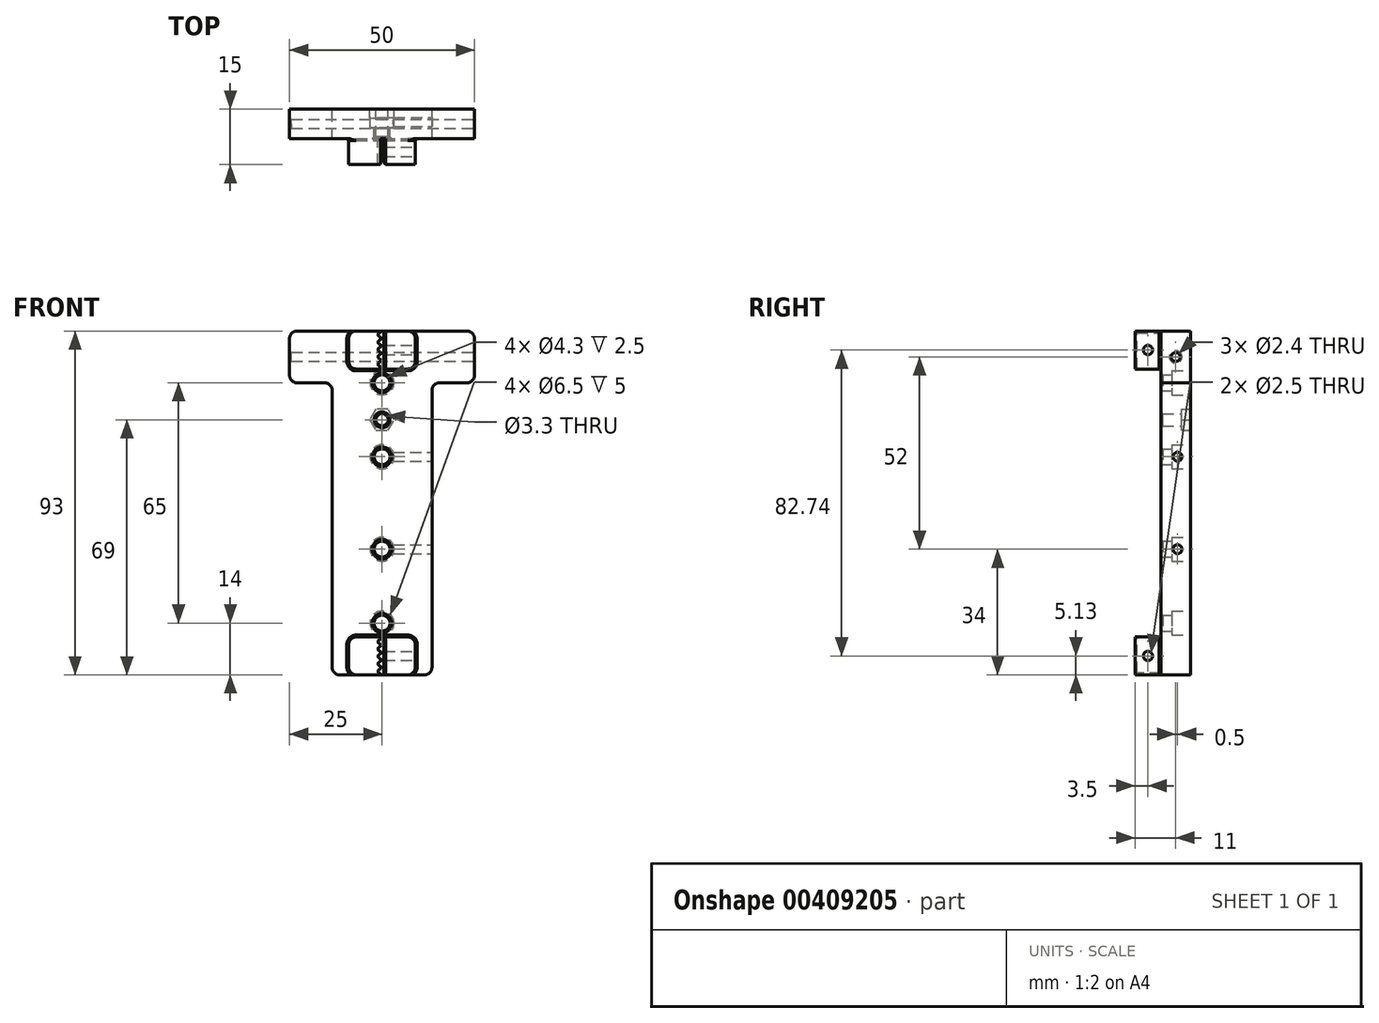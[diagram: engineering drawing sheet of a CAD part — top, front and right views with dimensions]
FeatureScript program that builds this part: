
annotation { "Feature Type Name" : "Feature", "Feature Type Description" : "" }
export const myFeature = defineFeature(function(context is Context, id is Id, definition is map)
    precondition{}
    {
        {
            var Q0;
            Q0=qCreatedBy(makeId("Front.planeOp"),FACE);
            var sketch = newSketch(context, id + "F0", { "sketchPlane" : qUnion([Q0])});
            skLineSegment(sketch, "E0.bottom", {"start": v(13.5, -86) * mm, "end": v(-13.5, -86) * mm});
            skLineSegment(sketch, "E0.left", {"start": v(13.5, -86) * mm, "end": v(13.5, -7) * mm});
            skLineSegment(sketch, "E0.right", {"start": v(-13.5, -86) * mm, "end": v(-13.5, -7) * mm});
            skLineSegment(sketch, "E1.top", {"start": v(-25, 7) * mm, "end": v(25, 7) * mm});
            skLineSegment(sketch, "E1.left", {"start": v(-25, -7) * mm, "end": v(-25, 7) * mm});
            skLineSegment(sketch, "E1.right", {"start": v(25, -7) * mm, "end": v(25, 7) * mm});
            skPoint(sketch, "E1.middle", {"position": v(0, 0) * mm});
            skCircle(sketch, "E2", {"center": v(0, -7) * mm, "radius": 2.15 * mm});
            skCircle(sketch, "E3", {"center": v(0, -17) * mm, "radius": 1.65 * mm});
            skCircle(sketch, "E4", {"center": v(0, -27) * mm, "radius": 2.15 * mm});
            skCircle(sketch, "E5", {"center": v(0, -52) * mm, "radius": 2.15 * mm});
            skCircle(sketch, "E6", {"center": v(0, -72) * mm, "radius": 2.15 * mm});
            skLineSegment(sketch, "E7", {"start": v(-32.04, -39.5) * mm, "end": v(39, -39.5) * mm, "construction": true});
            skLineSegment(sketch, "E8", {"start": v(-25, -7) * mm, "end": v(-13.5, -7) * mm});
            skLineSegment(sketch, "E9", {"start": v(13.5, -7) * mm, "end": v(25, -7) * mm});
            skSolve(sketch);
        }
        {
            var Q0;
            Q0=makeQuery(id+"F0.imprint","IMPRINT",FACE,{"disambiguationData":[TD([[makeQuery(id+"F0.imprint","IMPRINT",EDGE,{"derivedFrom":sQuery(id+"F0.wireOp",EDGE,"E0.bottom")}),-1.0]])]});
            extrude(context, id + "F1", {"entities" : qUnion([Q0]), "depth" : 8 * mm, "offsetDistance" : 25 * mm, "symmetric" : true});
        }
        {
            var Q0;
            Q0=makeQuery(id+"F1.opExtrude","CAP_FACE",FACE,{"disambiguationData":[OSD([sQuery(id+"F0.wireOp",EDGE,"E0.bottom"),sQuery(id+"F0.wireOp",EDGE,"E0.left"),sQuery(id+"F0.wireOp",EDGE,"E0.right"),sQuery(id+"F0.wireOp",EDGE,"E1.top"),sQuery(id+"F0.wireOp",EDGE,"E1.left"),sQuery(id+"F0.wireOp",EDGE,"E1.right"),sQuery(id+"F0.wireOp",EDGE,"E2"),sQuery(id+"F0.wireOp",EDGE,"E3"),sQuery(id+"F0.wireOp",EDGE,"E4"),sQuery(id+"F0.wireOp",EDGE,"E5"),sQuery(id+"F0.wireOp",EDGE,"E6"),sQuery(id+"F0.wireOp",EDGE,"E8"),sQuery(id+"F0.wireOp",EDGE,"E9")])],"isStart":false});
            var sketch = newSketch(context, id + "F2", { "sketchPlane" : qUnion([Q0])});
            skLineSegment(sketch, "E10", {"start": v(0.48, 7) * mm, "end": v(0.48, 6) * mm});
            skLineSegment(sketch, "E11", {"start": v(-0.35, 7) * mm, "end": v(-0.35, 6.74) * mm});
            skArc(sketch, "E12", {"start": v(-0.35, 6.74) * mm, "mid": v(-0.4, 6.64) * mm, "end": v(-0.48, 6.6) * mm});
            skLineSegment(sketch, "E13", {"start": v(-1.63, 6) * mm, "end": v(0.48, 6) * mm, "construction": true});
            skArc(sketch, "E14", {"start": v(-1.1, 6) * mm, "mid": v(-1.02, 6.3) * mm, "end": v(-0.8, 6.5) * mm});
            skArc(sketch, "E15", {"start": v(-0.8, 6.5) * mm, "mid": v(-0.64, 6.56) * mm, "end": v(-0.48, 6.6) * mm});
            skArc(sketch, "E16.MirrorCS", {"start": v(-1.1, 6) * mm, "mid": v(-1.02, 5.7) * mm, "end": v(-0.8, 5.5) * mm});
            skArc(sketch, "E17.MirrorCS", {"start": v(-0.8, 5.5) * mm, "mid": v(-0.64, 5.44) * mm, "end": v(-0.48, 5.4) * mm});
            skArc(sketch, "E18.MirrorCS", {"start": v(-0.35, 5.26) * mm, "mid": v(-0.4, 5.36) * mm, "end": v(-0.48, 5.4) * mm});
            skLineSegment(sketch, "E19.MirrorCS", {"start": v(-0.35, 5) * mm, "end": v(-0.35, 5.26) * mm});
            skLineSegment(sketch, "E20.MirrorCS", {"start": v(0.48, 5) * mm, "end": v(0.48, 6) * mm});
            skLineSegment(sketch, "E21", {"start": v(-0.35, 5) * mm, "end": v(0.48, 5) * mm, "construction": true});
            skArc(sketch, "E22.MirrorCS", {"start": v(-0.35, 3.26) * mm, "mid": v(-0.4, 3.36) * mm, "end": v(-0.48, 3.4) * mm});
            skArc(sketch, "E23.MirrorCS", {"start": v(-0.8, 3.5) * mm, "mid": v(-0.64, 3.44) * mm, "end": v(-0.48, 3.4) * mm});
            skLineSegment(sketch, "E24.MirrorCS", {"start": v(-0.35, 5) * mm, "end": v(-0.35, 4.74) * mm});
            skArc(sketch, "E25.MirrorCS", {"start": v(-0.8, 4.5) * mm, "mid": v(-0.64, 4.56) * mm, "end": v(-0.48, 4.6) * mm});
            skArc(sketch, "E26.MirrorCS", {"start": v(-0.35, 4.74) * mm, "mid": v(-0.4, 4.64) * mm, "end": v(-0.48, 4.6) * mm});
            skLineSegment(sketch, "E27.MirrorCS", {"start": v(-0.35, 3) * mm, "end": v(-0.35, 3.26) * mm});
            skLineSegment(sketch, "E28.MirrorCS", {"start": v(-1.63, 4) * mm, "end": v(0.48, 4) * mm, "construction": true});
            skArc(sketch, "E29.MirrorCS", {"start": v(-1.1, 4) * mm, "mid": v(-1.02, 4.3) * mm, "end": v(-0.8, 4.5) * mm});
            skLineSegment(sketch, "E30.MirrorCS", {"start": v(0.48, 3) * mm, "end": v(0.48, 4) * mm});
            skArc(sketch, "E31.MirrorCS", {"start": v(-1.1, 4) * mm, "mid": v(-1.02, 3.7) * mm, "end": v(-0.8, 3.5) * mm});
            skLineSegment(sketch, "E32.MirrorCS", {"start": v(0.48, 5) * mm, "end": v(0.48, 4) * mm});
            skLineSegment(sketch, "E33", {"start": v(-0.35, 3) * mm, "end": v(0.48, 3) * mm, "construction": true});
            skLineSegment(sketch, "E34.MirrorCS", {"start": v(-0.35, 1) * mm, "end": v(-0.35, 0.74) * mm});
            skArc(sketch, "E35.MirrorCS", {"start": v(-0.35, -0.74) * mm, "mid": v(-0.4, -0.64) * mm, "end": v(-0.48, -0.6) * mm});
            skArc(sketch, "E36.MirrorCS", {"start": v(-0.35, 2.74) * mm, "mid": v(-0.4, 2.64) * mm, "end": v(-0.48, 2.6) * mm});
            skArc(sketch, "E37.MirrorCS", {"start": v(-0.35, 0.74) * mm, "mid": v(-0.4, 0.64) * mm, "end": v(-0.48, 0.6) * mm});
            skArc(sketch, "E38.MirrorCS", {"start": v(-0.8, -0.5) * mm, "mid": v(-0.64, -0.56) * mm, "end": v(-0.48, -0.6) * mm});
            skArc(sketch, "E39.MirrorCS", {"start": v(-0.35, 1.26) * mm, "mid": v(-0.4, 1.36) * mm, "end": v(-0.48, 1.4) * mm});
            skArc(sketch, "E40.MirrorCS", {"start": v(-0.8, 2.5) * mm, "mid": v(-0.64, 2.56) * mm, "end": v(-0.48, 2.6) * mm});
            skLineSegment(sketch, "E41.MirrorCS", {"start": v(-0.35, 3) * mm, "end": v(-0.35, 2.74) * mm});
            skLineSegment(sketch, "E42.MirrorCS", {"start": v(-0.35, 1) * mm, "end": v(-0.35, 1.26) * mm});
            skArc(sketch, "E43.MirrorCS", {"start": v(-0.8, 0.5) * mm, "mid": v(-0.64, 0.56) * mm, "end": v(-0.48, 0.6) * mm});
            skArc(sketch, "E44.MirrorCS", {"start": v(-0.8, 1.5) * mm, "mid": v(-0.64, 1.44) * mm, "end": v(-0.48, 1.4) * mm});
            skLineSegment(sketch, "E45.MirrorCS", {"start": v(-0.35, -1) * mm, "end": v(-0.35, -0.74) * mm});
            skArc(sketch, "E46.MirrorCS", {"start": v(-1.1, 0) * mm, "mid": v(-1.02, -0.3) * mm, "end": v(-0.8, -0.5) * mm});
            skLineSegment(sketch, "E47.MirrorCS", {"start": v(-1.63, 0) * mm, "end": v(0.48, 0) * mm, "construction": true});
            skLineSegment(sketch, "E48.MirrorCS", {"start": v(-0.35, 1) * mm, "end": v(0.48, 1) * mm, "construction": true});
            skLineSegment(sketch, "E49.MirrorCS", {"start": v(0.48, 1) * mm, "end": v(0.48, 2) * mm});
            skArc(sketch, "E50.MirrorCS", {"start": v(-1.1, 2) * mm, "mid": v(-1.02, 2.3) * mm, "end": v(-0.8, 2.5) * mm});
            skArc(sketch, "E51.MirrorCS", {"start": v(-1.1, 2) * mm, "mid": v(-1.02, 1.7) * mm, "end": v(-0.8, 1.5) * mm});
            skLineSegment(sketch, "E52.MirrorCS", {"start": v(0.48, 1) * mm, "end": v(0.48, 0) * mm});
            skArc(sketch, "E53.MirrorCS", {"start": v(-1.1, 0) * mm, "mid": v(-1.02, 0.3) * mm, "end": v(-0.8, 0.5) * mm});
            skLineSegment(sketch, "E54.MirrorCS", {"start": v(0.48, -1) * mm, "end": v(0.48, 0) * mm});
            skLineSegment(sketch, "E55.MirrorCS", {"start": v(0.48, 3) * mm, "end": v(0.48, 2) * mm});
            skLineSegment(sketch, "E56.MirrorCS", {"start": v(-1.63, 2) * mm, "end": v(0.48, 2) * mm, "construction": true});
            skLineSegment(sketch, "E57", {"start": v(-0.35, -1) * mm, "end": v(0.48, -1) * mm, "construction": true});
            skLineSegment(sketch, "E58.MirrorCS", {"start": v(-0.35, -3) * mm, "end": v(-0.35, -2.74) * mm});
            skArc(sketch, "E59.MirrorCS", {"start": v(-0.35, -1.26) * mm, "mid": v(-0.4, -1.36) * mm, "end": v(-0.48, -1.4) * mm});
            skArc(sketch, "E60.MirrorCS", {"start": v(-0.35, -2.74) * mm, "mid": v(-0.4, -2.64) * mm, "end": v(-0.48, -2.6) * mm});
            skLineSegment(sketch, "E61.MirrorCS", {"start": v(-0.35, -3) * mm, "end": v(-0.35, -3.26) * mm});
            skLineSegment(sketch, "E62.MirrorCS", {"start": v(-0.35, -1) * mm, "end": v(-0.35, -1.26) * mm});
            skArc(sketch, "E63.MirrorCS", {"start": v(-0.8, -2.5) * mm, "mid": v(-0.64, -2.56) * mm, "end": v(-0.48, -2.6) * mm});
            skArc(sketch, "E64.MirrorCS", {"start": v(-0.8, -1.5) * mm, "mid": v(-0.64, -1.44) * mm, "end": v(-0.48, -1.4) * mm});
            skLineSegment(sketch, "E65.MirrorCS", {"start": v(-0.35, -3) * mm, "end": v(0.48, -3) * mm, "construction": true});
            skLineSegment(sketch, "E66.MirrorCS", {"start": v(0.48, -3) * mm, "end": v(0.48, -2) * mm});
            skLineSegment(sketch, "E67.MirrorCS", {"start": v(-1.63, -2) * mm, "end": v(0.48, -2) * mm, "construction": true});
            skArc(sketch, "E68.MirrorCS", {"start": v(-1.1, -2) * mm, "mid": v(-1.02, -2.3) * mm, "end": v(-0.8, -2.5) * mm});
            skLineSegment(sketch, "E69.MirrorCS", {"start": v(0.48, -1) * mm, "end": v(0.48, -2) * mm});
            skArc(sketch, "E70.MirrorCS", {"start": v(-1.1, -2) * mm, "mid": v(-1.02, -1.7) * mm, "end": v(-0.8, -1.5) * mm});
            skLineSegment(sketch, "E71", {"start": v(0.48, 7) * mm, "end": v(9, 7) * mm});
            skLineSegment(sketch, "E72", {"start": v(9, 7) * mm, "end": v(9, -3.26) * mm});
            skLineSegment(sketch, "E73", {"start": v(9, -3.26) * mm, "end": v(0.48, -3.26) * mm});
            skLineSegment(sketch, "E74", {"start": v(-0.35, 7) * mm, "end": v(-9, 7) * mm});
            skLineSegment(sketch, "E75", {"start": v(-9, 7) * mm, "end": v(-9, -3.26) * mm});
            skLineSegment(sketch, "E76", {"start": v(-9, -3.26) * mm, "end": v(-0.35, -3.26) * mm});
            skLineSegment(sketch, "E77", {"start": v(0.48, -3) * mm, "end": v(0.48, -3.26) * mm});
            skLineSegment(sketch, "E78", {"start": v(-13.5, -39.5) * mm, "end": v(13.5, -39.5) * mm, "construction": true});
            skArc(sketch, "E79.MirrorCS", {"start": v(-0.35, -83.74) * mm, "mid": v(-0.4, -83.64) * mm, "end": v(-0.48, -83.6) * mm});
            skLineSegment(sketch, "E80.MirrorCS", {"start": v(-0.35, -84) * mm, "end": v(-0.35, -84.26) * mm});
            skArc(sketch, "E81.MirrorCS", {"start": v(-0.35, -84.26) * mm, "mid": v(-0.4, -84.36) * mm, "end": v(-0.48, -84.4) * mm});
            skArc(sketch, "E82.MirrorCS", {"start": v(-0.8, -83.5) * mm, "mid": v(-0.64, -83.56) * mm, "end": v(-0.48, -83.6) * mm});
            skLineSegment(sketch, "E83.MirrorCS", {"start": v(-0.35, -84) * mm, "end": v(-0.35, -83.74) * mm});
            skArc(sketch, "E84.MirrorCS", {"start": v(-0.8, -84.5) * mm, "mid": v(-0.64, -84.44) * mm, "end": v(-0.48, -84.4) * mm});
            skArc(sketch, "E85.MirrorCS", {"start": v(-0.35, -80.26) * mm, "mid": v(-0.4, -80.36) * mm, "end": v(-0.48, -80.4) * mm});
            skArc(sketch, "E86.MirrorCS", {"start": v(-0.35, -79.74) * mm, "mid": v(-0.4, -79.64) * mm, "end": v(-0.48, -79.6) * mm});
            skArc(sketch, "E87.MirrorCS", {"start": v(-0.8, -80.5) * mm, "mid": v(-0.64, -80.44) * mm, "end": v(-0.48, -80.4) * mm});
            skArc(sketch, "E88.MirrorCS", {"start": v(-0.8, -79.5) * mm, "mid": v(-0.64, -79.56) * mm, "end": v(-0.48, -79.6) * mm});
            skLineSegment(sketch, "E89.MirrorCS", {"start": v(-0.35, -80) * mm, "end": v(-0.35, -79.74) * mm});
            skLineSegment(sketch, "E90.MirrorCS", {"start": v(-0.35, -80) * mm, "end": v(-0.35, -80.26) * mm});
            skLineSegment(sketch, "E91.MirrorCS", {"start": v(-0.35, -78) * mm, "end": v(-0.35, -77.74) * mm});
            skLineSegment(sketch, "E92.MirrorCS", {"start": v(-0.35, -78) * mm, "end": v(-0.35, -78.26) * mm});
            skArc(sketch, "E93.MirrorCS", {"start": v(-0.35, -82.26) * mm, "mid": v(-0.4, -82.36) * mm, "end": v(-0.48, -82.4) * mm});
            skArc(sketch, "E94.MirrorCS", {"start": v(-0.8, -78.5) * mm, "mid": v(-0.64, -78.44) * mm, "end": v(-0.48, -78.4) * mm});
            skArc(sketch, "E95.MirrorCS", {"start": v(-0.35, -78.26) * mm, "mid": v(-0.4, -78.36) * mm, "end": v(-0.48, -78.4) * mm});
            skLineSegment(sketch, "E96.MirrorCS", {"start": v(-0.35, -82) * mm, "end": v(-0.35, -82.26) * mm});
            skArc(sketch, "E97.MirrorCS", {"start": v(-0.8, -82.5) * mm, "mid": v(-0.64, -82.44) * mm, "end": v(-0.48, -82.4) * mm});
            skArc(sketch, "E98.MirrorCS", {"start": v(-0.8, -85.5) * mm, "mid": v(-0.64, -85.56) * mm, "end": v(-0.48, -85.6) * mm});
            skArc(sketch, "E99.MirrorCS", {"start": v(-0.35, -77.74) * mm, "mid": v(-0.4, -77.64) * mm, "end": v(-0.48, -77.6) * mm});
            skArc(sketch, "E100.MirrorCS", {"start": v(-1.1, -83) * mm, "mid": v(-1.02, -83.3) * mm, "end": v(-0.8, -83.5) * mm});
            skArc(sketch, "E101.MirrorCS", {"start": v(-0.8, -77.5) * mm, "mid": v(-0.64, -77.56) * mm, "end": v(-0.48, -77.6) * mm});
            skLineSegment(sketch, "E102.MirrorCS", {"start": v(-0.35, -82) * mm, "end": v(-0.35, -81.74) * mm});
            skArc(sketch, "E103.MirrorCS", {"start": v(-0.8, -76.5) * mm, "mid": v(-0.64, -76.44) * mm, "end": v(-0.48, -76.4) * mm});
            skLineSegment(sketch, "E104.MirrorCS", {"start": v(0.48, -76) * mm, "end": v(0.48, -75.74) * mm});
            skLineSegment(sketch, "E105.MirrorCS", {"start": v(-0.35, -76) * mm, "end": v(-0.35, -75.74) * mm});
            skLineSegment(sketch, "E106.MirrorCS", {"start": v(-0.35, -84) * mm, "end": v(0.48, -84) * mm, "construction": true});
            skArc(sketch, "E107.MirrorCS", {"start": v(-0.8, -81.5) * mm, "mid": v(-0.64, -81.56) * mm, "end": v(-0.48, -81.6) * mm});
            skArc(sketch, "E108.MirrorCS", {"start": v(-1.1, -83) * mm, "mid": v(-1.02, -82.7) * mm, "end": v(-0.8, -82.5) * mm});
            skLineSegment(sketch, "E109.MirrorCS", {"start": v(-1.63, -83) * mm, "end": v(0.48, -83) * mm, "construction": true});
            skArc(sketch, "E110.MirrorCS", {"start": v(-0.35, -85.74) * mm, "mid": v(-0.4, -85.64) * mm, "end": v(-0.48, -85.6) * mm});
            skArc(sketch, "E111.MirrorCS", {"start": v(-1.1, -85) * mm, "mid": v(-1.02, -85.3) * mm, "end": v(-0.8, -85.5) * mm});
            skArc(sketch, "E112.MirrorCS", {"start": v(-1.1, -81) * mm, "mid": v(-1.02, -80.7) * mm, "end": v(-0.8, -80.5) * mm});
            skArc(sketch, "E113.MirrorCS", {"start": v(-1.1, -85) * mm, "mid": v(-1.02, -84.7) * mm, "end": v(-0.8, -84.5) * mm});
            skLineSegment(sketch, "E114.MirrorCS", {"start": v(-0.35, -76) * mm, "end": v(-0.35, -76.26) * mm});
            skLineSegment(sketch, "E115.MirrorCS", {"start": v(-0.35, -86) * mm, "end": v(-0.35, -85.74) * mm});
            skLineSegment(sketch, "E116.MirrorCS", {"start": v(-0.35, -76) * mm, "end": v(0.48, -76) * mm, "construction": true});
            skArc(sketch, "E117.MirrorCS", {"start": v(-0.35, -81.74) * mm, "mid": v(-0.4, -81.64) * mm, "end": v(-0.48, -81.6) * mm});
            skLineSegment(sketch, "E118.MirrorCS", {"start": v(0.48, -84) * mm, "end": v(0.48, -85) * mm});
            skArc(sketch, "E119.MirrorCS", {"start": v(-1.1, -77) * mm, "mid": v(-1.02, -77.3) * mm, "end": v(-0.8, -77.5) * mm});
            skArc(sketch, "E120.MirrorCS", {"start": v(-0.35, -76.26) * mm, "mid": v(-0.4, -76.36) * mm, "end": v(-0.48, -76.4) * mm});
            skArc(sketch, "E121.MirrorCS", {"start": v(-1.1, -77) * mm, "mid": v(-1.02, -76.7) * mm, "end": v(-0.8, -76.5) * mm});
            skLineSegment(sketch, "E122.MirrorCS", {"start": v(0.48, -84) * mm, "end": v(0.48, -83) * mm});
            skArc(sketch, "E123.MirrorCS", {"start": v(-1.1, -79) * mm, "mid": v(-1.02, -79.3) * mm, "end": v(-0.8, -79.5) * mm});
            skLineSegment(sketch, "E124.MirrorCS", {"start": v(0.48, -82) * mm, "end": v(0.48, -83) * mm});
            skArc(sketch, "E125.MirrorCS", {"start": v(-1.1, -79) * mm, "mid": v(-1.02, -78.7) * mm, "end": v(-0.8, -78.5) * mm});
            skLineSegment(sketch, "E126.MirrorCS", {"start": v(0.48, -82) * mm, "end": v(0.48, -81) * mm});
            skLineSegment(sketch, "E127.MirrorCS", {"start": v(-0.35, -80) * mm, "end": v(0.48, -80) * mm, "construction": true});
            skLineSegment(sketch, "E128.MirrorCS", {"start": v(0.48, -78) * mm, "end": v(0.48, -77) * mm});
            skLineSegment(sketch, "E129.MirrorCS", {"start": v(0.48, -76) * mm, "end": v(0.48, -77) * mm});
            skLineSegment(sketch, "E130.MirrorCS", {"start": v(0.48, -80) * mm, "end": v(0.48, -79) * mm});
            skLineSegment(sketch, "E131.MirrorCS", {"start": v(-1.63, -85) * mm, "end": v(0.48, -85) * mm, "construction": true});
            skLineSegment(sketch, "E132.MirrorCS", {"start": v(-0.35, -78) * mm, "end": v(0.48, -78) * mm, "construction": true});
            skArc(sketch, "E133.MirrorCS", {"start": v(-1.1, -81) * mm, "mid": v(-1.02, -81.3) * mm, "end": v(-0.8, -81.5) * mm});
            skLineSegment(sketch, "E134.MirrorCS", {"start": v(0.48, -86) * mm, "end": v(0.48, -85) * mm});
            skLineSegment(sketch, "E135.MirrorCS", {"start": v(0.48, -80) * mm, "end": v(0.48, -81) * mm});
            skLineSegment(sketch, "E136.MirrorCS", {"start": v(0.48, -78) * mm, "end": v(0.48, -79) * mm});
            skLineSegment(sketch, "E137.MirrorCS", {"start": v(-0.35, -82) * mm, "end": v(0.48, -82) * mm, "construction": true});
            skLineSegment(sketch, "E138.MirrorCS", {"start": v(-1.63, -79) * mm, "end": v(0.48, -79) * mm, "construction": true});
            skLineSegment(sketch, "E139.MirrorCS", {"start": v(-1.63, -81) * mm, "end": v(0.48, -81) * mm, "construction": true});
            skLineSegment(sketch, "E140.MirrorCS", {"start": v(-1.63, -77) * mm, "end": v(0.48, -77) * mm, "construction": true});
            skLineSegment(sketch, "E141.MirrorCS", {"start": v(9, -86) * mm, "end": v(9, -75.74) * mm});
            skLineSegment(sketch, "E142.MirrorCS", {"start": v(0.48, -86) * mm, "end": v(9, -86) * mm});
            skLineSegment(sketch, "E143.MirrorCS", {"start": v(-9, -86) * mm, "end": v(-9, -75.74) * mm});
            skLineSegment(sketch, "E144.MirrorCS", {"start": v(-0.35, -86) * mm, "end": v(-9, -86) * mm});
            skLineSegment(sketch, "E145.MirrorCS", {"start": v(9, -75.74) * mm, "end": v(0.48, -75.74) * mm});
            skLineSegment(sketch, "E146.MirrorCS", {"start": v(-9, -75.74) * mm, "end": v(-0.35, -75.74) * mm});
            skSolve(sketch);
        }
        {
            var Q0;
            Q0 = qSketchRegion(id + "F2", true);
            extrude(context, id + "F3", {"entities" : qUnion([Q0]), "operationType" : NewBodyOperationType.ADD, "depth" : 7 * mm, "offsetDistance" : 25 * mm});
        }
        {
            var Q0;
            Q0=makeQuery(id+"F1.opExtrude","SWEPT_FACE",FACE,{"disambiguationData":[OSD([sQuery(id+"F0.wireOp",EDGE,"E1.right")])]});
            var sketch = newSketch(context, id + "F4", { "sketchPlane" : qUnion([Q0])});
            skCircle(sketch, "E147", {"center": v(0, 0) * mm, "radius": 1.2 * mm});
            skSolve(sketch);
        }
        {
            var Q0;
            Q0 = qSketchRegion(id + "F4", true);
            extrude(context, id + "F5", {"entities" : qUnion([Q0]), "operationType" : NewBodyOperationType.REMOVE, "endBound" : BoundingType.THROUGH_ALL, "oppositeDirection" : true, "depth" : 25 * mm});
        }
        {
            var Q0;
            Q0=makeQuery(id+"F1.opExtrude","SWEPT_FACE",FACE,{"disambiguationData":[OSD([sQuery(id+"F0.wireOp",EDGE,"E0.left")])]});
            var sketch = newSketch(context, id + "F6", { "sketchPlane" : qUnion([Q0])});
            skLineSegment(sketch, "E148.0", {"start": v(-4, -29.15) * mm, "end": v(-4, -24.85) * mm, "construction": true});
            skLineSegment(sketch, "E149.0", {"start": v(-4, -54.15) * mm, "end": v(-4, -49.85) * mm, "construction": true});
            skLineSegment(sketch, "E150", {"start": v(-4, -27) * mm, "end": v(4, -27) * mm, "construction": true});
            skLineSegment(sketch, "E151", {"start": v(-4, -52) * mm, "end": v(4, -52) * mm, "construction": true});
            skPoint(sketch, "E152.centerSnap0", {"position": v(0, -27) * mm});
            skPoint(sketch, "E153.centerSnap0", {"position": v(0, -52) * mm});
            skLineSegment(sketch, "E154", {"start": v(0.5, -27) * mm, "end": v(0.5, -52) * mm, "construction": true});
            skCircle(sketch, "E155", {"center": v(0.5, -27) * mm, "radius": 1.2 * mm});
            skCircle(sketch, "E156", {"center": v(0.5, -52) * mm, "radius": 1.2 * mm});
            skSolve(sketch);
        }
        {
            var Q0;
            Q0 = qSketchRegion(id + "F6", true);
            extrude(context, id + "F7", {"entities" : qUnion([Q0]), "operationType" : NewBodyOperationType.REMOVE, "oppositeDirection" : true, "depth" : 13.5 * mm});
        }
        {
            var Q0;
            Q0=makeQuery(id+"F1.opExtrude","CAP_FACE",FACE,{"disambiguationData":[OSD([sQuery(id+"F0.wireOp",EDGE,"E0.bottom"),sQuery(id+"F0.wireOp",EDGE,"E0.left"),sQuery(id+"F0.wireOp",EDGE,"E0.right"),sQuery(id+"F0.wireOp",EDGE,"E1.top"),sQuery(id+"F0.wireOp",EDGE,"E1.left"),sQuery(id+"F0.wireOp",EDGE,"E1.right"),sQuery(id+"F0.wireOp",EDGE,"E2"),sQuery(id+"F0.wireOp",EDGE,"E3"),sQuery(id+"F0.wireOp",EDGE,"E4"),sQuery(id+"F0.wireOp",EDGE,"E5"),sQuery(id+"F0.wireOp",EDGE,"E6"),sQuery(id+"F0.wireOp",EDGE,"E8"),sQuery(id+"F0.wireOp",EDGE,"E9")])],"isStart":true});
            var sketch = newSketch(context, id + "F8", { "sketchPlane" : qUnion([Q0])});
            skCircle(sketch, "E157", {"center": v(0, -7) * mm, "radius": 3.25 * mm});
            skCircle(sketch, "E158", {"center": v(0, -27) * mm, "radius": 3.25 * mm});
            skCircle(sketch, "E159", {"center": v(0, -52) * mm, "radius": 3.25 * mm});
            skCircle(sketch, "E160", {"center": v(0, -72) * mm, "radius": 3.25 * mm});
            skSolve(sketch);
        }
        {
            var Q0;
            Q0 = qSketchRegion(id + "F8", true);
            extrude(context, id + "F9", {"entities" : qUnion([Q0]), "operationType" : NewBodyOperationType.REMOVE, "oppositeDirection" : true, "depth" : 5 * mm});
        }
        {
            var Q0;
            Q0=makeQuery(id+"F1.opExtrude","CAP_FACE",FACE,{"disambiguationData":[OSD([sQuery(id+"F0.wireOp",EDGE,"E0.bottom"),sQuery(id+"F0.wireOp",EDGE,"E0.left"),sQuery(id+"F0.wireOp",EDGE,"E0.right"),sQuery(id+"F0.wireOp",EDGE,"E1.top"),sQuery(id+"F0.wireOp",EDGE,"E1.left"),sQuery(id+"F0.wireOp",EDGE,"E1.right"),sQuery(id+"F0.wireOp",EDGE,"E2"),sQuery(id+"F0.wireOp",EDGE,"E3"),sQuery(id+"F0.wireOp",EDGE,"E4"),sQuery(id+"F0.wireOp",EDGE,"E5"),sQuery(id+"F0.wireOp",EDGE,"E6"),sQuery(id+"F0.wireOp",EDGE,"E8"),sQuery(id+"F0.wireOp",EDGE,"E9")])],"isStart":true});
            var sketch = newSketch(context, id + "F10", { "sketchPlane" : qUnion([Q0])});
            skCircle(sketch, "E161.cCircle", {"center": v(0, -17) * mm, "radius": 3.3 * mm, "construction": true});
            skLineSegment(sketch, "E161.0", {"start": v(-3.3, -17) * mm, "end": v(-1.65, -14.15) * mm});
            skLineSegment(sketch, "E161.1", {"start": v(-1.65, -14.15) * mm, "end": v(1.65, -14.15) * mm});
            skLineSegment(sketch, "E161.2", {"start": v(1.65, -14.15) * mm, "end": v(3.3, -17) * mm});
            skLineSegment(sketch, "E161.3", {"start": v(3.3, -17) * mm, "end": v(1.65, -19.85) * mm});
            skLineSegment(sketch, "E161.4", {"start": v(1.65, -19.85) * mm, "end": v(-1.65, -19.85) * mm});
            skLineSegment(sketch, "E161.5", {"start": v(-1.65, -19.85) * mm, "end": v(-3.3, -17) * mm});
            skSolve(sketch);
        }
        {
            var Q0;
            Q0=makeQuery(id+"F10.imprint","IMPRINT",FACE,{"disambiguationData":[TD([[makeQuery(id+"F10.imprint","IMPRINT",EDGE,{"derivedFrom":sQuery(id+"F10.wireOp",EDGE,"E161.0")}),-1.0]])]});
            extrude(context, id + "F11", {"entities" : qUnion([Q0]), "operationType" : NewBodyOperationType.REMOVE, "oppositeDirection" : true, "depth" : 2.4 * mm});
        }
        {
            var Q0;
            Q0=makeQuery(id+"F1.opExtrude","SWEPT_EDGE",EDGE,{"disambiguationData":[OSD([sQuery(id+"F0.wireOp",EDGE,"E0.bottom"),sQuery(id+"F0.wireOp",EDGE,"E0.right")])]});
            var Q1;
            Q1=makeQuery(id+"F1.opExtrude","SWEPT_EDGE",EDGE,{"disambiguationData":[OSD([sQuery(id+"F0.wireOp",EDGE,"E0.bottom"),sQuery(id+"F0.wireOp",EDGE,"E0.left")])]});
            var Q2;
            Q2=makeQuery(id+"F3.opExtrude","SWEPT_EDGE",EDGE,{"disambiguationData":[OSD([sQuery(id+"F0.wireOp",EDGE,"E0.bottom"),sQuery(id+"F2.wireOp",EDGE,"E141.MirrorCS"),sQuery(id+"F2.wireOp",EDGE,"E142.MirrorCS")])]});
            var Q3;
            Q3=makeQuery(id+"F3.opExtrude","SWEPT_EDGE",EDGE,{"disambiguationData":[OSD([sQuery(id+"F0.wireOp",EDGE,"E0.bottom"),sQuery(id+"F2.wireOp",EDGE,"E143.MirrorCS"),sQuery(id+"F2.wireOp",EDGE,"E144.MirrorCS")])]});
            var Q4;
            Q4=makeQuery(id+"F3.opExtrude","SWEPT_EDGE",EDGE,{"disambiguationData":[OSD([sQuery(id+"F2.wireOp",EDGE,"E72"),sQuery(id+"F2.wireOp",EDGE,"E73")])]});
            var Q5;
            Q5=makeQuery(id+"F3.opExtrude","SWEPT_EDGE",EDGE,{"disambiguationData":[OSD([sQuery(id+"F2.wireOp",EDGE,"E75"),sQuery(id+"F2.wireOp",EDGE,"E76")])]});
            var Q6;
            Q6=makeQuery(id+"F1.opExtrude","SWEPT_EDGE",EDGE,{"disambiguationData":[OSD([sQuery(id+"F0.wireOp",EDGE,"E1.right"),sQuery(id+"F0.wireOp",EDGE,"E9")])]});
            var Q7;
            Q7=makeQuery(id+"F1.opExtrude","SWEPT_EDGE",EDGE,{"disambiguationData":[OSD([sQuery(id+"F0.wireOp",EDGE,"E0.left"),sQuery(id+"F0.wireOp",EDGE,"E9")])]});
            var Q8;
            Q8=makeQuery(id+"F3.opExtrude","SWEPT_EDGE",EDGE,{"disambiguationData":[OSD([sQuery(id+"F2.wireOp",EDGE,"E141.MirrorCS"),sQuery(id+"F2.wireOp",EDGE,"E145.MirrorCS")])]});
            var Q9;
            Q9=makeQuery(id+"F3.opExtrude","SWEPT_EDGE",EDGE,{"disambiguationData":[OSD([sQuery(id+"F2.wireOp",EDGE,"E143.MirrorCS"),sQuery(id+"F2.wireOp",EDGE,"E146.MirrorCS")])]});
            var Q10;
            Q10=makeQuery(id+"F1.opExtrude","SWEPT_EDGE",EDGE,{"disambiguationData":[OSD([sQuery(id+"F0.wireOp",EDGE,"E0.right"),sQuery(id+"F0.wireOp",EDGE,"E8")])]});
            var Q11;
            Q11=makeQuery(id+"F1.opExtrude","SWEPT_EDGE",EDGE,{"disambiguationData":[OSD([sQuery(id+"F0.wireOp",EDGE,"E1.left"),sQuery(id+"F0.wireOp",EDGE,"E8")])]});
            var Q12;
            Q12=makeQuery(id+"F1.opExtrude","SWEPT_EDGE",EDGE,{"disambiguationData":[OSD([sQuery(id+"F0.wireOp",EDGE,"E1.top"),sQuery(id+"F0.wireOp",EDGE,"E1.left")])]});
            var Q13;
            Q13=makeQuery(id+"F1.opExtrude","SWEPT_EDGE",EDGE,{"disambiguationData":[OSD([sQuery(id+"F0.wireOp",EDGE,"E1.top"),sQuery(id+"F0.wireOp",EDGE,"E1.right")])]});
            var Q14;
            Q14=makeQuery(id+"F3.opExtrude","SWEPT_EDGE",EDGE,{"disambiguationData":[OSD([sQuery(id+"F0.wireOp",EDGE,"E1.top"),sQuery(id+"F2.wireOp",EDGE,"E71"),sQuery(id+"F2.wireOp",EDGE,"E72")])]});
            var Q15;
            Q15=makeQuery(id+"F3.opExtrude","SWEPT_EDGE",EDGE,{"disambiguationData":[OSD([sQuery(id+"F0.wireOp",EDGE,"E1.top"),sQuery(id+"F2.wireOp",EDGE,"E74"),sQuery(id+"F2.wireOp",EDGE,"E75")])]});
            fillet(context, id + "F12", {"entities" : qUnion([Q0, Q1, Q2, Q3, Q4, Q5, Q6, Q7, Q8, Q9, Q10, Q11, Q12, Q13, Q14, Q15]), "radius" : 2 * mm, "tangentPropagation" : true, "allowEdgeOverflow" : false});
        }
        {
            var Q0;
            Q0=makeQuery(id+"F3.opExtrude","SWEPT_FACE",FACE,{"disambiguationData":[OSD([sQuery(id+"F2.wireOp",EDGE,"E72")])]});
            var sketch = newSketch(context, id + "F13", { "sketchPlane" : qUnion([Q0])});
            skCircle(sketch, "E162", {"center": v(-7.5, 1.87) * mm, "radius": 1.25 * mm});
            skCircle(sketch, "E163", {"center": v(-7.5, -80.87) * mm, "radius": 1.25 * mm});
            skSolve(sketch);
        }
        {
            var Q0;
            Q0=makeQuery(id+"F13.imprint","IMPRINT",FACE,{"disambiguationData":[TD([[makeQuery(id+"F13.imprint","IMPRINT",EDGE,{"derivedFrom":sQuery(id+"F13.wireOp",EDGE,"E162")}),1.0]])]});
            var Q1;
            Q1=makeQuery(id+"F13.imprint","IMPRINT",FACE,{"disambiguationData":[TD([[makeQuery(id+"F13.imprint","IMPRINT",EDGE,{"derivedFrom":sQuery(id+"F13.wireOp",EDGE,"E163")}),1.0]])]});
            extrude(context, id + "F14", {"entities" : qUnion([Q0, Q1]), "operationType" : NewBodyOperationType.REMOVE, "endBound" : BoundingType.UP_TO_NEXT, "oppositeDirection" : true, "depth" : 25 * mm, "offsetDistance" : 25 * mm});
        }
        {
            var Q0;
            Q0=makeQuery(id+"F5.boolean.opBoolean","INTERSECT",EDGE,{"derivedFrom":[makeQuery(id+"F1.opExtrude","SWEPT_FACE",FACE,{"disambiguationData":[OSD([sQuery(id+"F0.wireOp",EDGE,"E1.left")])]}),makeQuery(id+"F5.opExtrude","SWEPT_FACE",FACE,{"disambiguationData":[OSD([sQuery(id+"F4.wireOp",EDGE,"E147")])]})]});
            var Q1;
            Q1=makeQuery(id+"F5.boolean.opBoolean","COPY",EDGE,{"derivedFrom":makeQuery(id+"F5.opExtrude","CAP_EDGE",EDGE,{"disambiguationData":[OSD([sQuery(id+"F4.wireOp",EDGE,"E147")])],"isStart":true})});
            var Q2;
            Q2=makeQuery(id+"F14.boolean.opBoolean","COPY",EDGE,{"derivedFrom":makeQuery(id+"F14.opExtrude","CAP_EDGE",EDGE,{"disambiguationData":[OSD([sQuery(id+"F13.wireOp",EDGE,"E162")])],"isStart":true})});
            var Q3;
            Q3=makeQuery(id+"F7.boolean.opBoolean","COPY",EDGE,{"derivedFrom":makeQuery(id+"F7.opExtrude","CAP_EDGE",EDGE,{"disambiguationData":[OSD([sQuery(id+"F6.wireOp",EDGE,"E155")])],"isStart":true})});
            var Q4;
            Q4=makeQuery(id+"F7.boolean.opBoolean","COPY",EDGE,{"derivedFrom":makeQuery(id+"F7.opExtrude","CAP_EDGE",EDGE,{"disambiguationData":[OSD([sQuery(id+"F6.wireOp",EDGE,"E156")])],"isStart":true})});
            var Q5;
            Q5=makeQuery(id+"F14.boolean.opBoolean","COPY",EDGE,{"derivedFrom":makeQuery(id+"F14.opExtrude","CAP_EDGE",EDGE,{"disambiguationData":[OSD([sQuery(id+"F13.wireOp",EDGE,"E163")])],"isStart":true})});
            var Q6;
            Q6=makeQuery(id+"F3.opExtrude","CAP_EDGE",EDGE,{"disambiguationData":[OSD([sQuery(id+"F2.wireOp",EDGE,"E10"),sQuery(id+"F2.wireOp",EDGE,"E20.MirrorCS"),sQuery(id+"F2.wireOp",EDGE,"E30.MirrorCS"),sQuery(id+"F2.wireOp",EDGE,"E32.MirrorCS"),sQuery(id+"F2.wireOp",EDGE,"E49.MirrorCS"),sQuery(id+"F2.wireOp",EDGE,"E52.MirrorCS"),sQuery(id+"F2.wireOp",EDGE,"E54.MirrorCS"),sQuery(id+"F2.wireOp",EDGE,"E55.MirrorCS"),sQuery(id+"F2.wireOp",EDGE,"E66.MirrorCS"),sQuery(id+"F2.wireOp",EDGE,"E69.MirrorCS"),sQuery(id+"F2.wireOp",EDGE,"E77")])],"isStart":false});
            var Q7;
            Q7=makeQuery(id+"F3.opExtrude","SWEPT_EDGE",EDGE,{"disambiguationData":[OSD([sQuery(id+"F0.wireOp",EDGE,"E1.top"),sQuery(id+"F2.wireOp",EDGE,"E10"),sQuery(id+"F2.wireOp",EDGE,"E71")])]});
            var Q8;
            Q8=makeQuery(id+"F14.boolean.opBoolean","COPY",EDGE,{"derivedFrom":makeQuery(id+"F14.opExtrude","TWEAK_EDGE",EDGE,{"derivedFrom":[makeQuery(id+"F3.opExtrude","SWEPT_FACE",FACE,{"disambiguationData":[OSD([sQuery(id+"F2.wireOp",EDGE,"E10"),sQuery(id+"F2.wireOp",EDGE,"E20.MirrorCS"),sQuery(id+"F2.wireOp",EDGE,"E30.MirrorCS"),sQuery(id+"F2.wireOp",EDGE,"E32.MirrorCS"),sQuery(id+"F2.wireOp",EDGE,"E49.MirrorCS"),sQuery(id+"F2.wireOp",EDGE,"E52.MirrorCS"),sQuery(id+"F2.wireOp",EDGE,"E54.MirrorCS"),sQuery(id+"F2.wireOp",EDGE,"E55.MirrorCS"),sQuery(id+"F2.wireOp",EDGE,"E66.MirrorCS"),sQuery(id+"F2.wireOp",EDGE,"E69.MirrorCS"),sQuery(id+"F2.wireOp",EDGE,"E77")])]}),makeQuery(id+"F13.imprint","IMPRINT",EDGE,{"derivedFrom":sQuery(id+"F13.wireOp",EDGE,"E162")})]})});
            var Q9;
            Q9=makeQuery(id+"F3.opExtrude","SWEPT_EDGE",EDGE,{"disambiguationData":[OSD([sQuery(id+"F0.wireOp",EDGE,"E0.bottom"),sQuery(id+"F2.wireOp",EDGE,"E134.MirrorCS"),sQuery(id+"F2.wireOp",EDGE,"E142.MirrorCS")])]});
            var Q10;
            Q10=makeQuery(id+"F14.boolean.opBoolean","COPY",EDGE,{"derivedFrom":makeQuery(id+"F14.opExtrude","TWEAK_EDGE",EDGE,{"derivedFrom":[makeQuery(id+"F3.opExtrude","SWEPT_FACE",FACE,{"disambiguationData":[OSD([sQuery(id+"F2.wireOp",EDGE,"E104.MirrorCS"),sQuery(id+"F2.wireOp",EDGE,"E118.MirrorCS"),sQuery(id+"F2.wireOp",EDGE,"E122.MirrorCS"),sQuery(id+"F2.wireOp",EDGE,"E124.MirrorCS"),sQuery(id+"F2.wireOp",EDGE,"E126.MirrorCS"),sQuery(id+"F2.wireOp",EDGE,"E128.MirrorCS"),sQuery(id+"F2.wireOp",EDGE,"E129.MirrorCS"),sQuery(id+"F2.wireOp",EDGE,"E130.MirrorCS"),sQuery(id+"F2.wireOp",EDGE,"E134.MirrorCS"),sQuery(id+"F2.wireOp",EDGE,"E135.MirrorCS"),sQuery(id+"F2.wireOp",EDGE,"E136.MirrorCS")])]}),makeQuery(id+"F13.imprint","IMPRINT",EDGE,{"derivedFrom":sQuery(id+"F13.wireOp",EDGE,"E163")})]})});
            var Q11;
            Q11=makeQuery(id+"F3.opExtrude","CAP_EDGE",EDGE,{"disambiguationData":[OSD([sQuery(id+"F2.wireOp",EDGE,"E104.MirrorCS"),sQuery(id+"F2.wireOp",EDGE,"E118.MirrorCS"),sQuery(id+"F2.wireOp",EDGE,"E122.MirrorCS"),sQuery(id+"F2.wireOp",EDGE,"E124.MirrorCS"),sQuery(id+"F2.wireOp",EDGE,"E126.MirrorCS"),sQuery(id+"F2.wireOp",EDGE,"E128.MirrorCS"),sQuery(id+"F2.wireOp",EDGE,"E129.MirrorCS"),sQuery(id+"F2.wireOp",EDGE,"E130.MirrorCS"),sQuery(id+"F2.wireOp",EDGE,"E134.MirrorCS"),sQuery(id+"F2.wireOp",EDGE,"E135.MirrorCS"),sQuery(id+"F2.wireOp",EDGE,"E136.MirrorCS")])],"isStart":false});
            var Q12;
            Q12=makeQuery(id+"F1.opExtrude","CAP_EDGE",EDGE,{"disambiguationData":[OSD([sQuery(id+"F0.wireOp",EDGE,"E2")])],"isStart":false});
            var Q13;
            Q13=makeQuery(id+"F1.opExtrude","CAP_EDGE",EDGE,{"disambiguationData":[OSD([sQuery(id+"F0.wireOp",EDGE,"E3")])],"isStart":false});
            var Q14;
            Q14=makeQuery(id+"F1.opExtrude","CAP_EDGE",EDGE,{"disambiguationData":[OSD([sQuery(id+"F0.wireOp",EDGE,"E4")])],"isStart":false});
            var Q15;
            Q15=makeQuery(id+"F1.opExtrude","CAP_EDGE",EDGE,{"disambiguationData":[OSD([sQuery(id+"F0.wireOp",EDGE,"E5")])],"isStart":false});
            var Q16;
            Q16=makeQuery(id+"F1.opExtrude","CAP_EDGE",EDGE,{"disambiguationData":[OSD([sQuery(id+"F0.wireOp",EDGE,"E6")])],"isStart":false});
            var Q17;
            {var subQ0=sQuery(id+"F0.wireOp",EDGE,"E1.top");Q17=makeQuery(id+"F12.opFillet","BLEND_EDGE",EDGE,{"blendedFrom":[makeQuery(id+"F3.opExtrude","SWEPT_EDGE",EDGE,{"disambiguationData":[OSD([subQ0,sQuery(id+"F2.wireOp",EDGE,"E71"),sQuery(id+"F2.wireOp",EDGE,"E72")])]}),makeQuery(id+"F1.opExtrude","CAP_FACE",FACE,{"disambiguationData":[OSD([sQuery(id+"F0.wireOp",EDGE,"E0.bottom"),sQuery(id+"F0.wireOp",EDGE,"E0.left"),sQuery(id+"F0.wireOp",EDGE,"E0.right"),subQ0,sQuery(id+"F0.wireOp",EDGE,"E1.left"),sQuery(id+"F0.wireOp",EDGE,"E1.right"),sQuery(id+"F0.wireOp",EDGE,"E2"),sQuery(id+"F0.wireOp",EDGE,"E3"),sQuery(id+"F0.wireOp",EDGE,"E4"),sQuery(id+"F0.wireOp",EDGE,"E5"),sQuery(id+"F0.wireOp",EDGE,"E6"),sQuery(id+"F0.wireOp",EDGE,"E8"),sQuery(id+"F0.wireOp",EDGE,"E9")])],"isStart":false})],"blendedInto":[makeQuery(id+"F1.opExtrude","CAP_FACE",FACE,{"disambiguationData":[OSD([sQuery(id+"F0.wireOp",EDGE,"E0.bottom"),sQuery(id+"F0.wireOp",EDGE,"E0.left"),sQuery(id+"F0.wireOp",EDGE,"E0.right"),subQ0,sQuery(id+"F0.wireOp",EDGE,"E1.left"),sQuery(id+"F0.wireOp",EDGE,"E1.right"),sQuery(id+"F0.wireOp",EDGE,"E2"),sQuery(id+"F0.wireOp",EDGE,"E3"),sQuery(id+"F0.wireOp",EDGE,"E4"),sQuery(id+"F0.wireOp",EDGE,"E5"),sQuery(id+"F0.wireOp",EDGE,"E6"),sQuery(id+"F0.wireOp",EDGE,"E8"),sQuery(id+"F0.wireOp",EDGE,"E9")])],"isStart":false})]});}
            var Q18;
            Q18=makeQuery(id+"F12.opFillet","BLEND_EDGE",EDGE,{"blendedFrom":[makeQuery(id+"F3.opExtrude","SWEPT_EDGE",EDGE,{"disambiguationData":[OSD([sQuery(id+"F2.wireOp",EDGE,"E75"),sQuery(id+"F2.wireOp",EDGE,"E76")])]}),makeQuery(id+"F1.opExtrude","CAP_FACE",FACE,{"disambiguationData":[OSD([sQuery(id+"F0.wireOp",EDGE,"E0.bottom"),sQuery(id+"F0.wireOp",EDGE,"E0.left"),sQuery(id+"F0.wireOp",EDGE,"E0.right"),sQuery(id+"F0.wireOp",EDGE,"E1.top"),sQuery(id+"F0.wireOp",EDGE,"E1.left"),sQuery(id+"F0.wireOp",EDGE,"E1.right"),sQuery(id+"F0.wireOp",EDGE,"E2"),sQuery(id+"F0.wireOp",EDGE,"E3"),sQuery(id+"F0.wireOp",EDGE,"E4"),sQuery(id+"F0.wireOp",EDGE,"E5"),sQuery(id+"F0.wireOp",EDGE,"E6"),sQuery(id+"F0.wireOp",EDGE,"E8"),sQuery(id+"F0.wireOp",EDGE,"E9")])],"isStart":false})],"blendedInto":[makeQuery(id+"F1.opExtrude","CAP_FACE",FACE,{"disambiguationData":[OSD([sQuery(id+"F0.wireOp",EDGE,"E0.bottom"),sQuery(id+"F0.wireOp",EDGE,"E0.left"),sQuery(id+"F0.wireOp",EDGE,"E0.right"),sQuery(id+"F0.wireOp",EDGE,"E1.top"),sQuery(id+"F0.wireOp",EDGE,"E1.left"),sQuery(id+"F0.wireOp",EDGE,"E1.right"),sQuery(id+"F0.wireOp",EDGE,"E2"),sQuery(id+"F0.wireOp",EDGE,"E3"),sQuery(id+"F0.wireOp",EDGE,"E4"),sQuery(id+"F0.wireOp",EDGE,"E5"),sQuery(id+"F0.wireOp",EDGE,"E6"),sQuery(id+"F0.wireOp",EDGE,"E8"),sQuery(id+"F0.wireOp",EDGE,"E9")])],"isStart":false})]});
            var Q19;
            Q19=makeQuery(id+"F12.opFillet","BLEND_EDGE",EDGE,{"blendedFrom":[makeQuery(id+"F3.opExtrude","SWEPT_EDGE",EDGE,{"disambiguationData":[OSD([sQuery(id+"F2.wireOp",EDGE,"E143.MirrorCS"),sQuery(id+"F2.wireOp",EDGE,"E146.MirrorCS")])]}),makeQuery(id+"F1.opExtrude","CAP_FACE",FACE,{"disambiguationData":[OSD([sQuery(id+"F0.wireOp",EDGE,"E0.bottom"),sQuery(id+"F0.wireOp",EDGE,"E0.left"),sQuery(id+"F0.wireOp",EDGE,"E0.right"),sQuery(id+"F0.wireOp",EDGE,"E1.top"),sQuery(id+"F0.wireOp",EDGE,"E1.left"),sQuery(id+"F0.wireOp",EDGE,"E1.right"),sQuery(id+"F0.wireOp",EDGE,"E2"),sQuery(id+"F0.wireOp",EDGE,"E3"),sQuery(id+"F0.wireOp",EDGE,"E4"),sQuery(id+"F0.wireOp",EDGE,"E5"),sQuery(id+"F0.wireOp",EDGE,"E6"),sQuery(id+"F0.wireOp",EDGE,"E8"),sQuery(id+"F0.wireOp",EDGE,"E9")])],"isStart":false})],"blendedInto":[makeQuery(id+"F1.opExtrude","CAP_FACE",FACE,{"disambiguationData":[OSD([sQuery(id+"F0.wireOp",EDGE,"E0.bottom"),sQuery(id+"F0.wireOp",EDGE,"E0.left"),sQuery(id+"F0.wireOp",EDGE,"E0.right"),sQuery(id+"F0.wireOp",EDGE,"E1.top"),sQuery(id+"F0.wireOp",EDGE,"E1.left"),sQuery(id+"F0.wireOp",EDGE,"E1.right"),sQuery(id+"F0.wireOp",EDGE,"E2"),sQuery(id+"F0.wireOp",EDGE,"E3"),sQuery(id+"F0.wireOp",EDGE,"E4"),sQuery(id+"F0.wireOp",EDGE,"E5"),sQuery(id+"F0.wireOp",EDGE,"E6"),sQuery(id+"F0.wireOp",EDGE,"E8"),sQuery(id+"F0.wireOp",EDGE,"E9")])],"isStart":false})]});
            var Q20;
            Q20=makeQuery(id+"F12.opFillet","BLEND_EDGE",EDGE,{"blendedFrom":[makeQuery(id+"F3.opExtrude","SWEPT_EDGE",EDGE,{"disambiguationData":[OSD([sQuery(id+"F2.wireOp",EDGE,"E141.MirrorCS"),sQuery(id+"F2.wireOp",EDGE,"E145.MirrorCS")])]}),makeQuery(id+"F1.opExtrude","CAP_FACE",FACE,{"disambiguationData":[OSD([sQuery(id+"F0.wireOp",EDGE,"E0.bottom"),sQuery(id+"F0.wireOp",EDGE,"E0.left"),sQuery(id+"F0.wireOp",EDGE,"E0.right"),sQuery(id+"F0.wireOp",EDGE,"E1.top"),sQuery(id+"F0.wireOp",EDGE,"E1.left"),sQuery(id+"F0.wireOp",EDGE,"E1.right"),sQuery(id+"F0.wireOp",EDGE,"E2"),sQuery(id+"F0.wireOp",EDGE,"E3"),sQuery(id+"F0.wireOp",EDGE,"E4"),sQuery(id+"F0.wireOp",EDGE,"E5"),sQuery(id+"F0.wireOp",EDGE,"E6"),sQuery(id+"F0.wireOp",EDGE,"E8"),sQuery(id+"F0.wireOp",EDGE,"E9")])],"isStart":false})],"blendedInto":[makeQuery(id+"F1.opExtrude","CAP_FACE",FACE,{"disambiguationData":[OSD([sQuery(id+"F0.wireOp",EDGE,"E0.bottom"),sQuery(id+"F0.wireOp",EDGE,"E0.left"),sQuery(id+"F0.wireOp",EDGE,"E0.right"),sQuery(id+"F0.wireOp",EDGE,"E1.top"),sQuery(id+"F0.wireOp",EDGE,"E1.left"),sQuery(id+"F0.wireOp",EDGE,"E1.right"),sQuery(id+"F0.wireOp",EDGE,"E2"),sQuery(id+"F0.wireOp",EDGE,"E3"),sQuery(id+"F0.wireOp",EDGE,"E4"),sQuery(id+"F0.wireOp",EDGE,"E5"),sQuery(id+"F0.wireOp",EDGE,"E6"),sQuery(id+"F0.wireOp",EDGE,"E8"),sQuery(id+"F0.wireOp",EDGE,"E9")])],"isStart":false})]});
            chamfer(context, id + "F15", {"entities" : qUnion([Q0, Q1, Q2, Q3, Q4, Q5, Q6, Q7, Q8, Q9, Q10, Q11, Q12, Q13, Q14, Q15, Q16, Q17, Q18, Q19, Q20]), "width" : 0.5 * mm, "tangentPropagation" : true});
        }
    });
